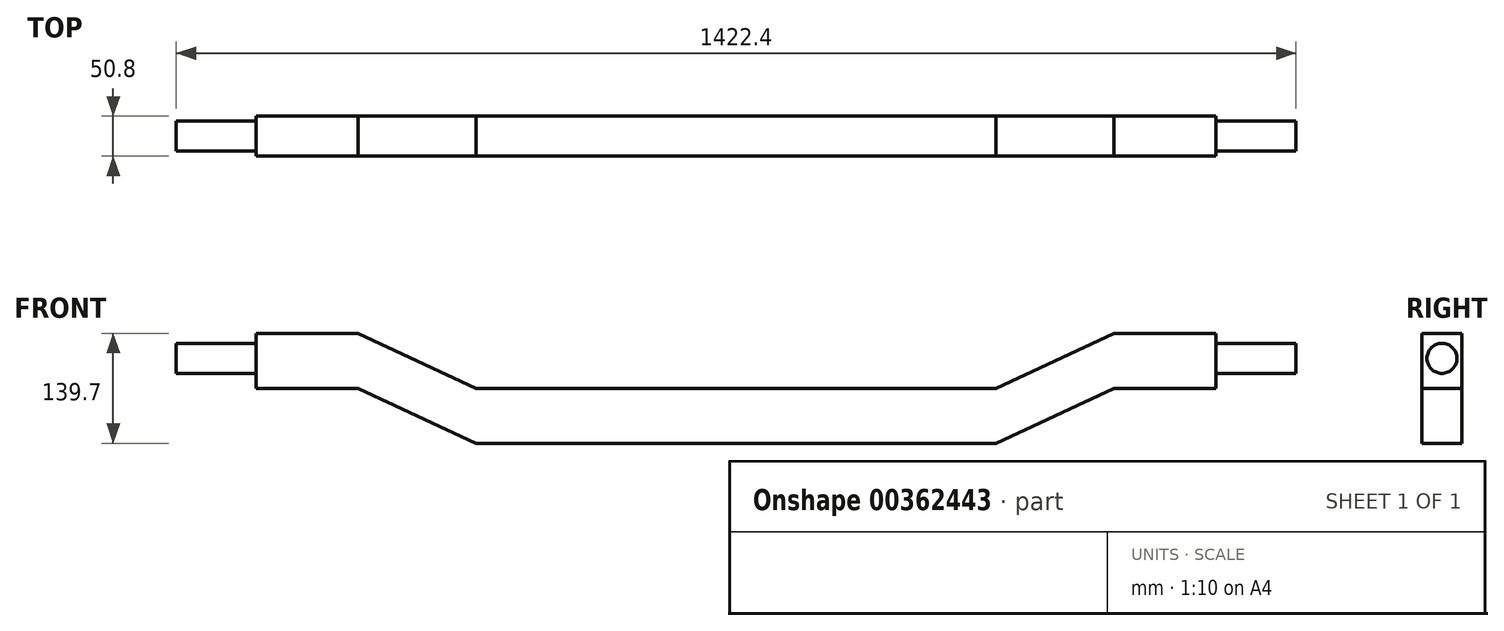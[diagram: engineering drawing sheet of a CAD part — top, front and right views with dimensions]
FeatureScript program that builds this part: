
annotation { "Feature Type Name" : "Feature", "Feature Type Description" : "" }
export const myFeature = defineFeature(function(context is Context, id is Id, definition is map)
    precondition{}
    {
        {
            var Q0;
            Q0=qCreatedBy(makeId("Front.planeOp"),FACE);
            var sketch = newSketch(context, id + "F0", { "sketchPlane" : qUnion([Q0])});
            skLineSegment(sketch, "E0", {"start": v(0, 0) * mm, "end": v(330.2, 0) * mm});
            skLineSegment(sketch, "E1", {"start": v(330.2, 0) * mm, "end": v(480, 69.85) * mm});
            skLineSegment(sketch, "E2", {"start": v(480, 69.85) * mm, "end": v(609.6, 69.85) * mm});
            skLineSegment(sketch, "E3", {"start": v(609.6, 69.85) * mm, "end": v(609.6, 139.7) * mm});
            skLineSegment(sketch, "E4", {"start": v(609.6, 139.7) * mm, "end": v(480, 139.7) * mm});
            skLineSegment(sketch, "E5", {"start": v(480, 139.7) * mm, "end": v(330.2, 69.85) * mm});
            skLineSegment(sketch, "E6", {"start": v(330.2, 69.85) * mm, "end": v(0, 69.85) * mm});
            skLineSegment(sketch, "E7", {"start": v(0, 69.85) * mm, "end": v(0, 0) * mm});
            skSolve(sketch);
        }
        {
            var Q0;
            Q0 = qSketchRegion(id + "F0", true);
            extrude(context, id + "F1", {"entities" : qUnion([Q0]), "depth" : 50.8 * mm});
        }
        {
            var Q0;
            Q0=makeQuery(id+"F1.opExtrude","SWEPT_BODY",BODY,{"disambiguationData":[OSD([sQuery(id+"F0.wireOp",EDGE,"E0"),sQuery(id+"F0.wireOp",EDGE,"E1"),sQuery(id+"F0.wireOp",EDGE,"E2"),sQuery(id+"F0.wireOp",EDGE,"E3"),sQuery(id+"F0.wireOp",EDGE,"E4"),sQuery(id+"F0.wireOp",EDGE,"E5"),sQuery(id+"F0.wireOp",EDGE,"E6"),sQuery(id+"F0.wireOp",EDGE,"E7")])]});
            var Q1;
            Q1=qCreatedBy(makeId("Right.planeOp"),FACE);
            mirror(context, id + "F2", {"operationType" : NewBodyOperationType.ADD, "entities" : qUnion([Q0]), "mirrorPlane" : qUnion([Q1])});
        }
        {
            var Q0;
            Q0=makeQuery(id+"F1.opExtrude","SWEPT_FACE",FACE,{"disambiguationData":[OSD([sQuery(id+"F0.wireOp",EDGE,"E3")])]});
            var sketch = newSketch(context, id + "F3", { "sketchPlane" : qUnion([Q0])});
            skCircle(sketch, "E8", {"center": v(-25.4, 107.95) * mm, "radius": 19.05 * mm});
            skSolve(sketch);
        }
        {
            var Q0;
            Q0 = qSketchRegion(id + "F3", true);
            extrude(context, id + "F4", {"entities" : qUnion([Q0]), "operationType" : NewBodyOperationType.ADD, "depth" : 101.6 * mm});
        }
        {
            var Q0;
            Q0=makeQuery(id+"F1.opExtrude","SWEPT_BODY",BODY,{"disambiguationData":[OSD([sQuery(id+"F0.wireOp",EDGE,"E0"),sQuery(id+"F0.wireOp",EDGE,"E1"),sQuery(id+"F0.wireOp",EDGE,"E2"),sQuery(id+"F0.wireOp",EDGE,"E3"),sQuery(id+"F0.wireOp",EDGE,"E4"),sQuery(id+"F0.wireOp",EDGE,"E5"),sQuery(id+"F0.wireOp",EDGE,"E6"),sQuery(id+"F0.wireOp",EDGE,"E7")])]});
            var Q1;
            Q1=qCreatedBy(makeId("Right.planeOp"),FACE);
            mirror(context, id + "F5", {"operationType" : NewBodyOperationType.ADD, "entities" : qUnion([Q0]), "mirrorPlane" : qUnion([Q1])});
        }
    });
